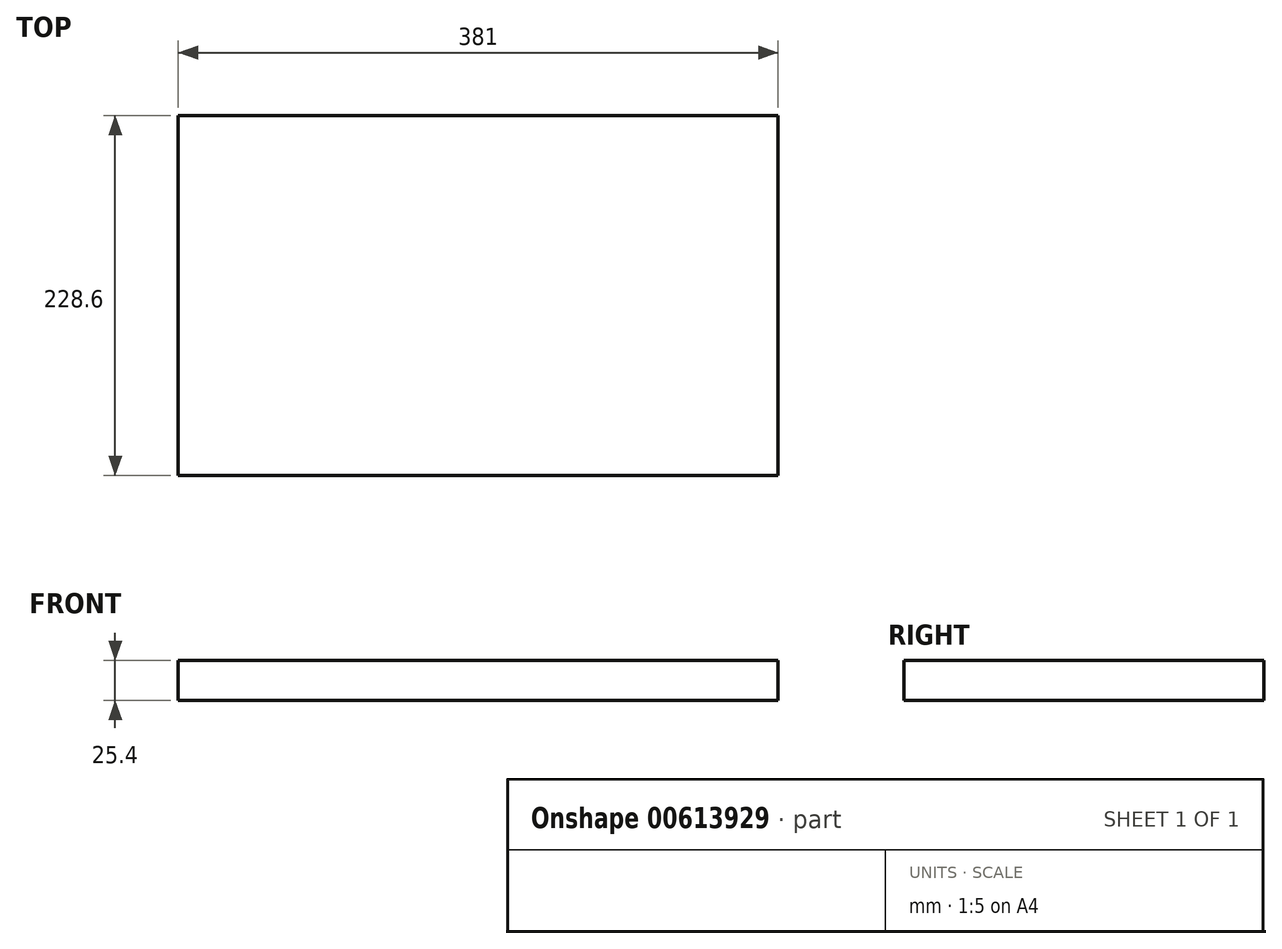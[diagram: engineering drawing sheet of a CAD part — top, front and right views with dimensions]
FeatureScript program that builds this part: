
annotation { "Feature Type Name" : "Feature", "Feature Type Description" : "" }
export const myFeature = defineFeature(function(context is Context, id is Id, definition is map)
    precondition{}
    {
        {
            var Q0;
            Q0=qCreatedBy(makeId("Top.planeOp"),FACE);
            var sketch = newSketch(context, id + "F0", { "sketchPlane" : qUnion([Q0])});
            skLineSegment(sketch, "E0.bottom", {"start": v(-189.64, -158.14) * mm, "end": v(191.36, -158.14) * mm});
            skLineSegment(sketch, "E0.top", {"start": v(-189.64, 70.46) * mm, "end": v(191.36, 70.46) * mm});
            skLineSegment(sketch, "E0.left", {"start": v(-189.64, -158.14) * mm, "end": v(-189.64, 70.46) * mm});
            skLineSegment(sketch, "E0.right", {"start": v(191.36, -158.14) * mm, "end": v(191.36, 70.46) * mm});
            skSolve(sketch);
        }
        {
            var Q0;
            Q0 = qSketchRegion(id + "F0", true);
            extrude(context, id + "F1", {"entities" : qUnion([Q0]), "depth" : 25.4 * mm, "offsetDistance" : 25.4 * mm});
        }
    });
